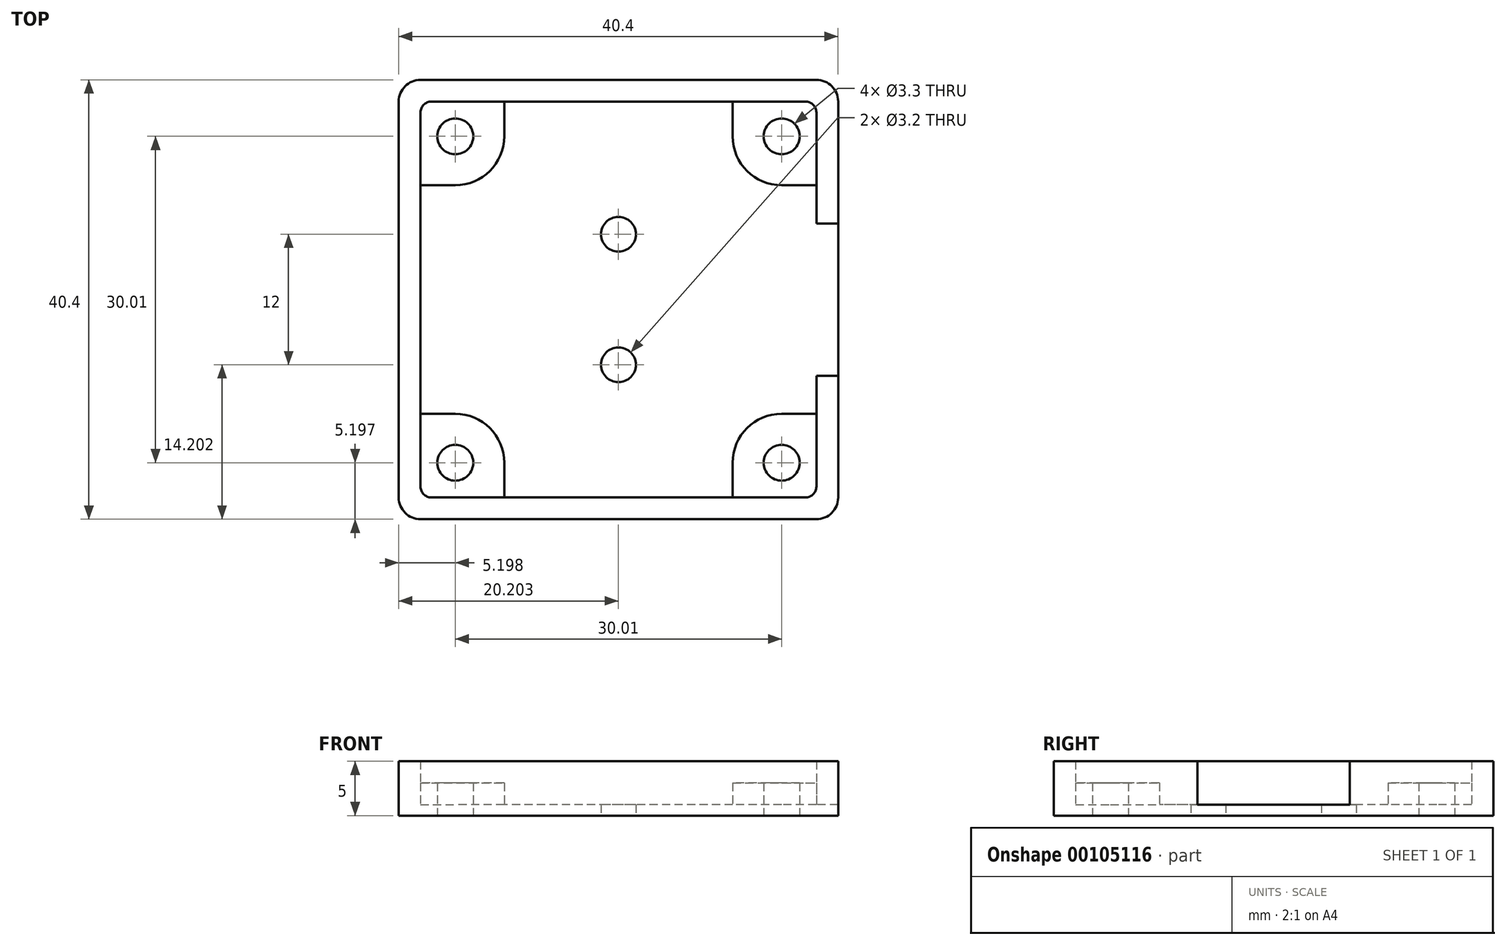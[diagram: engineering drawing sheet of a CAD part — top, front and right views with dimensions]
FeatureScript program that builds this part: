
annotation { "Feature Type Name" : "Feature", "Feature Type Description" : "" }
export const myFeature = defineFeature(function(context is Context, id is Id, definition is map)
    precondition{}
    {
        {
            var Q0;
            Q0=qCreatedBy(makeId("Top.planeOp"),FACE);
            var sketch = newSketch(context, id + "F0", { "sketchPlane" : qUnion([Q0])});
            skLineSegment(sketch, "E0.bottom", {"start": v(-25.1, -4.44) * mm, "end": v(11.3, -4.44) * mm});
            skLineSegment(sketch, "E0.top", {"start": v(-25.1, 31.96) * mm, "end": v(11.3, 31.96) * mm});
            skLineSegment(sketch, "E0.left", {"start": v(-25.1, -4.44) * mm, "end": v(-25.1, 31.96) * mm});
            skLineSegment(sketch, "E0.right", {"start": v(11.3, -4.44) * mm, "end": v(11.3, 31.96) * mm});
            skLineSegment(sketch, "E1", {"start": v(-25.1, 31.96) * mm, "end": v(11.3, -4.44) * mm, "construction": true});
            skLineSegment(sketch, "E2", {"start": v(11.3, 31.96) * mm, "end": v(-25.1, -4.44) * mm, "construction": true});
            skPoint(sketch, "E3", {"position": v(-6.9, 13.76) * mm});
            skCircle(sketch, "E4", {"center": v(-21.91, 28.77) * mm, "radius": 1.65 * mm});
            skLineSegment(sketch, "E5.0", {"start": v(-27.1, -6.44) * mm, "end": v(13.3, -6.44) * mm});
            skLineSegment(sketch, "E5.1", {"start": v(-27.1, -6.44) * mm, "end": v(-27.1, 33.96) * mm});
            skLineSegment(sketch, "E5.2", {"start": v(-27.1, 33.96) * mm, "end": v(13.3, 33.96) * mm});
            skLineSegment(sketch, "E5.3", {"start": v(13.3, -6.44) * mm, "end": v(13.3, 33.96) * mm});
            skLineSegment(sketch, "E6.anchor1", {"start": v(-6.9, 13.76) * mm, "end": v(-21.91, 28.77) * mm, "construction": true});
            skLineSegment(sketch, "E6.anchor2", {"start": v(-6.9, 13.76) * mm, "end": v(-23.88, -3.2) * mm, "construction": true});
            skLineSegment(sketch, "E7", {"start": v(-17.41, 28.77) * mm, "end": v(-17.41, 31.96) * mm});
            skLineSegment(sketch, "E8", {"start": v(-21.91, 24.27) * mm, "end": v(-25.1, 24.27) * mm});
            skArc(sketch, "E9", {"start": v(-17.41, 28.77) * mm, "mid": v(-25.1, 31.95) * mm, "end": v(-21.91, 24.27) * mm, "construction": true});
            skArc(sketch, "E10", {"start": v(-21.91, 24.27) * mm, "mid": v(-18.73, 25.58) * mm, "end": v(-17.41, 28.77) * mm});
            skCircle(sketch, "E11.1.0", {"center": v(-21.91, -1.24) * mm, "radius": 1.65 * mm});
            skArc(sketch, "E11.1.1", {"start": v(-17.41, -1.24) * mm, "mid": v(-18.73, 1.94) * mm, "end": v(-21.91, 3.26) * mm});
            skLineSegment(sketch, "E11.1.2", {"start": v(-21.91, 3.26) * mm, "end": v(-25.1, 3.26) * mm});
            skLineSegment(sketch, "E11.1.3", {"start": v(-17.41, -1.24) * mm, "end": v(-17.41, -4.44) * mm});
            skCircle(sketch, "E11.2.0", {"center": v(8.1, -1.24) * mm, "radius": 1.65 * mm});
            skArc(sketch, "E11.2.1", {"start": v(8.1, 3.26) * mm, "mid": v(4.92, 1.94) * mm, "end": v(3.6, -1.24) * mm});
            skLineSegment(sketch, "E11.2.2", {"start": v(3.6, -1.24) * mm, "end": v(3.6, -4.44) * mm});
            skLineSegment(sketch, "E11.2.3", {"start": v(8.1, 3.26) * mm, "end": v(11.3, 3.26) * mm});
            skCircle(sketch, "E11.3.0", {"center": v(8.1, 28.77) * mm, "radius": 1.65 * mm});
            skArc(sketch, "E11.3.1", {"start": v(3.6, 28.77) * mm, "mid": v(4.92, 25.58) * mm, "end": v(8.1, 24.27) * mm});
            skLineSegment(sketch, "E11.3.2", {"start": v(8.1, 24.27) * mm, "end": v(11.3, 24.27) * mm});
            skLineSegment(sketch, "E11.3.3", {"start": v(3.6, 28.77) * mm, "end": v(3.6, 31.96) * mm});
            skLineSegment(sketch, "E12", {"start": v(-6.9, 3.1) * mm, "end": v(-6.9, 27.97) * mm, "construction": true});
            skCircle(sketch, "E13", {"center": v(-6.9, 19.76) * mm, "radius": 1.6 * mm});
            skCircle(sketch, "E14", {"center": v(-6.9, 7.76) * mm, "radius": 1.6 * mm});
            skLineSegment(sketch, "E15", {"start": v(13.3, 13.76) * mm, "end": v(11.3, 13.76) * mm});
            skLineSegment(sketch, "E16", {"start": v(11.3, 20.76) * mm, "end": v(13.3, 20.76) * mm});
            skLineSegment(sketch, "E17", {"start": v(11.3, 6.76) * mm, "end": v(13.3, 6.76) * mm});
            skSolve(sketch);
        }
        {
            var Q0;
            Q0=makeQuery(id+"F0.imprint","IMPRINT",FACE,{"disambiguationData":[TD([[makeQuery(id+"F0.imprint","IMPRINT",EDGE,{"derivedFrom":sQuery(id+"F0.wireOp",EDGE,"E0.bottom")}),1.0]])]});
            var Q1;
            Q1=makeQuery(id+"F0.imprint","IMPRINT",FACE,{"disambiguationData":[TD([[makeQuery(id+"F0.imprint","IMPRINT",EDGE,{"derivedFrom":sQuery(id+"F0.wireOp",EDGE,"E0.bottom")}),-1.0]])]});
            var Q2;
            {var subQ2=sQuery(id+"F0.wireOp",EDGE,"E7");Q2=makeQuery(id+"F0.imprint","IMPRINT",FACE,{"disambiguationData":[TD([[makeQuery(id+"F0.imprint","IMPRINT",EDGE,{"derivedFrom":subQ2}),-1.0]])]});}
            var Q3;
            Q3=makeQuery(id+"F0.imprint","IMPRINT",FACE,{"disambiguationData":[TD([[makeQuery(id+"F0.imprint","IMPRINT",EDGE,{"derivedFrom":sQuery(id+"F0.wireOp",EDGE,"E4")}),-1.0]])]});
            var Q4;
            Q4=makeQuery(id+"F0.imprint","IMPRINT",FACE,{"disambiguationData":[TD([[makeQuery(id+"F0.imprint","IMPRINT",EDGE,{"derivedFrom":sQuery(id+"F0.wireOp",EDGE,"E11.3.0")}),-1.0]])]});
            var Q5;
            {var subQ0=sQuery(id+"F0.wireOp",EDGE,"E15");Q5=makeQuery(id+"F0.imprint","IMPRINT",FACE,{"disambiguationData":[TD([[makeQuery(id+"F0.imprint","IMPRINT",EDGE,{"derivedFrom":subQ0}),-1.0]])]});}
            var Q6;
            {var subQ0=sQuery(id+"F0.wireOp",EDGE,"E15");Q6=makeQuery(id+"F0.imprint","IMPRINT",FACE,{"disambiguationData":[TD([[makeQuery(id+"F0.imprint","IMPRINT",EDGE,{"derivedFrom":subQ0}),1.0]])]});}
            extrude(context, id + "F1", {"entities" : qUnion([Q0, Q1, Q2, Q3, Q4, Q5, Q6]), "depth" : 1 * mm});
        }
        {
            var Q0;
            Q0=makeQuery(id+"F0.imprint","IMPRINT",FACE,{"disambiguationData":[TD([[makeQuery(id+"F0.imprint","IMPRINT",EDGE,{"derivedFrom":sQuery(id+"F0.wireOp",EDGE,"E0.bottom")}),-1.0]])]});
            extrude(context, id + "F2", {"entities" : qUnion([Q0]), "operationType" : NewBodyOperationType.ADD, "depth" : 5 * mm});
        }
        {
            var Q0;
            Q0=makeQuery(id+"F0.imprint","IMPRINT",FACE,{"disambiguationData":[TD([[makeQuery(id+"F0.imprint","IMPRINT",EDGE,{"derivedFrom":sQuery(id+"F0.wireOp",EDGE,"E4")}),-1.0]])]});
            var Q1;
            Q1=makeQuery(id+"F0.imprint","IMPRINT",FACE,{"disambiguationData":[TD([[makeQuery(id+"F0.imprint","IMPRINT",EDGE,{"derivedFrom":sQuery(id+"F0.wireOp",EDGE,"E11.1.0")}),-1.0]])]});
            var Q2;
            Q2=makeQuery(id+"F0.imprint","IMPRINT",FACE,{"disambiguationData":[TD([[makeQuery(id+"F0.imprint","IMPRINT",EDGE,{"derivedFrom":sQuery(id+"F0.wireOp",EDGE,"E11.3.0")}),-1.0]])]});
            var Q3;
            Q3=makeQuery(id+"F0.imprint","IMPRINT",FACE,{"disambiguationData":[TD([[makeQuery(id+"F0.imprint","IMPRINT",EDGE,{"derivedFrom":sQuery(id+"F0.wireOp",EDGE,"E11.2.0")}),-1.0]])]});
            extrude(context, id + "F3", {"entities" : qUnion([Q0, Q1, Q2, Q3]), "operationType" : NewBodyOperationType.ADD, "depth" : 3 * mm});
        }
        {
            var Q0;
            {var subQ0=sQuery(id+"F0.wireOp",EDGE,"E5.1");var subQ1=sQuery(id+"F0.wireOp",EDGE,"E5.0");Q0=makeQuery(id+"F2.boolean.opBoolean","MERGE",EDGE,{"derivedFrom":[makeQuery(id+"F1.opExtrude","SWEPT_EDGE",EDGE,{"disambiguationData":[OSD([subQ1,subQ0])]}),makeQuery(id+"F2.opExtrude","SWEPT_EDGE",EDGE,{"disambiguationData":[OSD([subQ1,subQ0])]})]});}
            var Q1;
            {var subQ0=sQuery(id+"F0.wireOp",EDGE,"E5.3");var subQ1=sQuery(id+"F0.wireOp",EDGE,"E5.0");Q1=makeQuery(id+"F2.boolean.opBoolean","MERGE",EDGE,{"derivedFrom":[makeQuery(id+"F1.opExtrude","SWEPT_EDGE",EDGE,{"disambiguationData":[OSD([subQ1,subQ0])]}),makeQuery(id+"F2.opExtrude","SWEPT_EDGE",EDGE,{"disambiguationData":[OSD([subQ1,subQ0])]})]});}
            var Q2;
            {var subQ0=sQuery(id+"F0.wireOp",EDGE,"E5.3");var subQ1=sQuery(id+"F0.wireOp",EDGE,"E5.2");Q2=makeQuery(id+"F2.boolean.opBoolean","MERGE",EDGE,{"derivedFrom":[makeQuery(id+"F1.opExtrude","SWEPT_EDGE",EDGE,{"disambiguationData":[OSD([subQ1,subQ0])]}),makeQuery(id+"F2.opExtrude","SWEPT_EDGE",EDGE,{"disambiguationData":[OSD([subQ1,subQ0])]})]});}
            var Q3;
            {var subQ0=sQuery(id+"F0.wireOp",EDGE,"E5.2");var subQ1=sQuery(id+"F0.wireOp",EDGE,"E5.1");Q3=makeQuery(id+"F2.boolean.opBoolean","MERGE",EDGE,{"derivedFrom":[makeQuery(id+"F1.opExtrude","SWEPT_EDGE",EDGE,{"disambiguationData":[OSD([subQ1,subQ0])]}),makeQuery(id+"F2.opExtrude","SWEPT_EDGE",EDGE,{"disambiguationData":[OSD([subQ1,subQ0])]})]});}
            fillet(context, id + "F4", {"entities" : qUnion([Q0, Q1, Q2, Q3]), "radius" : 2 * mm, "tangentPropagation" : true, "allowEdgeOverflow" : false});
        }
        {
            var Q0;
            Q0=makeQuery(id+"F2.opExtrude","SWEPT_EDGE",EDGE,{"disambiguationData":[OSD([sQuery(id+"F0.wireOp",EDGE,"E0.top"),sQuery(id+"F0.wireOp",EDGE,"E0.left")])]});
            var Q1;
            Q1=makeQuery(id+"F2.opExtrude","SWEPT_EDGE",EDGE,{"disambiguationData":[OSD([sQuery(id+"F0.wireOp",EDGE,"E0.top"),sQuery(id+"F0.wireOp",EDGE,"E0.right")])]});
            var Q2;
            Q2=makeQuery(id+"F2.opExtrude","SWEPT_EDGE",EDGE,{"disambiguationData":[OSD([sQuery(id+"F0.wireOp",EDGE,"E0.bottom"),sQuery(id+"F0.wireOp",EDGE,"E0.right")])]});
            var Q3;
            Q3=makeQuery(id+"F2.opExtrude","SWEPT_EDGE",EDGE,{"disambiguationData":[OSD([sQuery(id+"F0.wireOp",EDGE,"E0.bottom"),sQuery(id+"F0.wireOp",EDGE,"E0.left")])]});
            fillet(context, id + "F5", {"entities" : qUnion([Q0, Q1, Q2, Q3]), "radius" : 1 * mm, "tangentPropagation" : true, "allowEdgeOverflow" : false});
        }
    });
